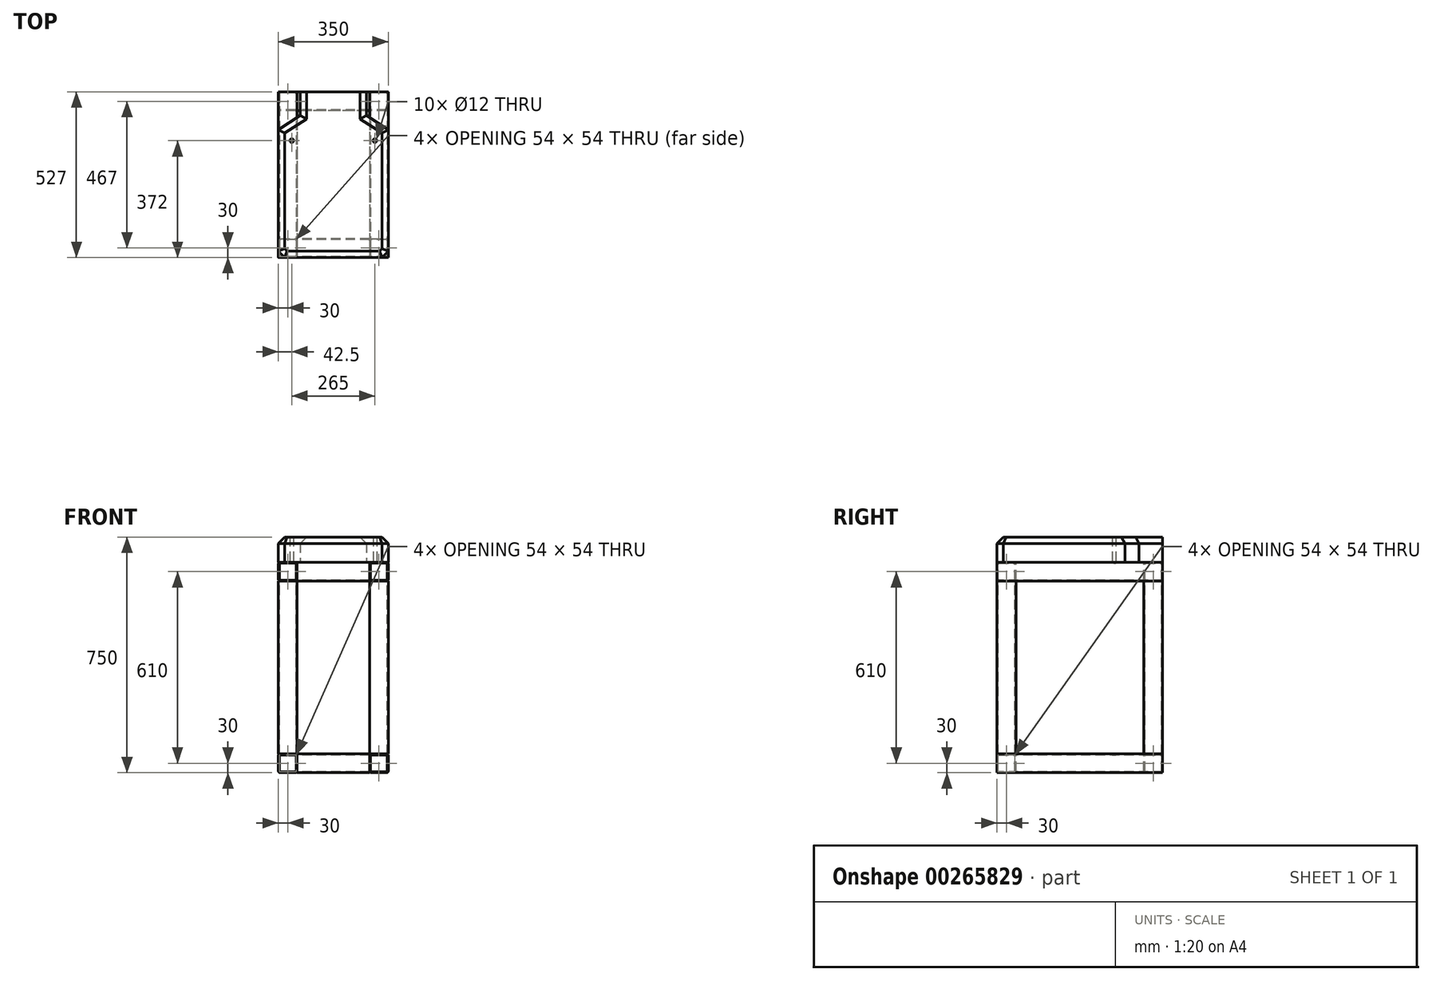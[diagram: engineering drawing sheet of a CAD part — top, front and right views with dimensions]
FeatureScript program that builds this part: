
annotation { "Feature Type Name" : "Feature", "Feature Type Description" : "" }
export const myFeature = defineFeature(function(context is Context, id is Id, definition is map)
    precondition{}
    {
        {
            var Q0;
            Q0=qCreatedBy(makeId("Top.planeOp"),FACE);
            var sketch = newSketch(context, id + "F0", { "sketchPlane" : qUnion([Q0])});
            skLineSegment(sketch, "E0.bottom", {"start": v(175, -263.5) * mm, "end": v(-175, -263.5) * mm});
            skLineSegment(sketch, "E0.top", {"start": v(105, 263.5) * mm, "end": v(-105, 263.5) * mm});
            skLineSegment(sketch, "E0.left", {"start": v(175, -263.5) * mm, "end": v(175, 143.5) * mm});
            skLineSegment(sketch, "E0.right", {"start": v(-175, -263.5) * mm, "end": v(-175, 143.5) * mm});
            skPoint(sketch, "E0.middle", {"position": v(0, 0) * mm});
            skCircle(sketch, "E1", {"center": v(-132.5, 108.5) * mm, "radius": 6 * mm});
            skCircle(sketch, "E2", {"center": v(132.5, 108.5) * mm, "radius": 6 * mm});
            skLineSegment(sketch, "E3", {"start": v(-175, 143.5) * mm, "end": v(-105, 188.5) * mm});
            skLineSegment(sketch, "E4", {"start": v(-105, 188.5) * mm, "end": v(-105, 263.5) * mm});
            skLineSegment(sketch, "E5", {"start": v(105, 263.5) * mm, "end": v(105, 188.5) * mm});
            skLineSegment(sketch, "E6", {"start": v(105, 188.5) * mm, "end": v(175, 143.5) * mm});
            skPoint(sketch, "E7.orphan", {"position": v(-175, 263.5) * mm});
            skPoint(sketch, "E8.orphan", {"position": v(175, 263.5) * mm});
            skSolve(sketch);
        }
        {
            var Q0;
            Q0 = qSketchRegion(id + "F0", true);
            extrude(context, id + "F1", {"entities" : qUnion([Q0]), "depth" : 80 * mm});
        }
        {
            var Q0;
            Q0=makeQuery(id+"F1.opExtrude","SWEPT_EDGE",EDGE,{"disambiguationData":[OSD([sQuery(id+"F0.wireOp",EDGE,"E0.bottom"),sQuery(id+"F0.wireOp",EDGE,"E0.right")])]});
            var Q1;
            Q1=makeQuery(id+"F1.opExtrude","SWEPT_EDGE",EDGE,{"disambiguationData":[OSD([sQuery(id+"F0.wireOp",EDGE,"E0.bottom"),sQuery(id+"F0.wireOp",EDGE,"E0.left")])]});
            chamfer(context, id + "F2", {"entities" : qUnion([Q0, Q1]), "width" : 20 * mm, "tangentPropagation" : true});
        }
        {
            var Q0;
            Q0=makeQuery(id+"F1.opExtrude","CAP_EDGE",EDGE,{"disambiguationData":[OSD([sQuery(id+"F0.wireOp",EDGE,"E0.right")])],"isStart":false});
            var Q1;
            Q1=makeQuery(id+"F1.opExtrude","CAP_EDGE",EDGE,{"disambiguationData":[OSD([sQuery(id+"F0.wireOp",EDGE,"E0.bottom")])],"isStart":false});
            var Q2;
            Q2=makeQuery(id+"F1.opExtrude","CAP_EDGE",EDGE,{"disambiguationData":[OSD([sQuery(id+"F0.wireOp",EDGE,"E0.left")])],"isStart":false});
            var Q3;
            {var subQ0=sQuery(id+"F0.wireOp",EDGE,"E0.left");var subQ1=sQuery(id+"F0.wireOp",EDGE,"E0.bottom");Q3=makeQuery(id+"F2.opChamfer","BLEND_EDGE",EDGE,{"blendedFrom":[makeQuery(id+"F1.opExtrude","SWEPT_EDGE",EDGE,{"disambiguationData":[OSD([subQ1,subQ0])]}),makeQuery(id+"F1.opExtrude","CAP_FACE",FACE,{"disambiguationData":[OSD([subQ1,sQuery(id+"F0.wireOp",EDGE,"E0.top"),subQ0,sQuery(id+"F0.wireOp",EDGE,"E0.right"),sQuery(id+"F0.wireOp",EDGE,"E1"),sQuery(id+"F0.wireOp",EDGE,"E2"),sQuery(id+"F0.wireOp",EDGE,"E3"),sQuery(id+"F0.wireOp",EDGE,"E4"),sQuery(id+"F0.wireOp",EDGE,"E5"),sQuery(id+"F0.wireOp",EDGE,"E6")])],"isStart":false})],"blendedInto":[makeQuery(id+"F1.opExtrude","CAP_FACE",FACE,{"disambiguationData":[OSD([subQ1,sQuery(id+"F0.wireOp",EDGE,"E0.top"),subQ0,sQuery(id+"F0.wireOp",EDGE,"E0.right"),sQuery(id+"F0.wireOp",EDGE,"E1"),sQuery(id+"F0.wireOp",EDGE,"E2"),sQuery(id+"F0.wireOp",EDGE,"E3"),sQuery(id+"F0.wireOp",EDGE,"E4"),sQuery(id+"F0.wireOp",EDGE,"E5"),sQuery(id+"F0.wireOp",EDGE,"E6")])],"isStart":false})]});}
            var Q4;
            {var subQ0=sQuery(id+"F0.wireOp",EDGE,"E0.right");var subQ1=sQuery(id+"F0.wireOp",EDGE,"E0.bottom");Q4=makeQuery(id+"F2.opChamfer","BLEND_EDGE",EDGE,{"blendedFrom":[makeQuery(id+"F1.opExtrude","SWEPT_EDGE",EDGE,{"disambiguationData":[OSD([subQ1,subQ0])]}),makeQuery(id+"F1.opExtrude","CAP_FACE",FACE,{"disambiguationData":[OSD([subQ1,sQuery(id+"F0.wireOp",EDGE,"E0.top"),sQuery(id+"F0.wireOp",EDGE,"E0.left"),subQ0,sQuery(id+"F0.wireOp",EDGE,"E1"),sQuery(id+"F0.wireOp",EDGE,"E2"),sQuery(id+"F0.wireOp",EDGE,"E3"),sQuery(id+"F0.wireOp",EDGE,"E4"),sQuery(id+"F0.wireOp",EDGE,"E5"),sQuery(id+"F0.wireOp",EDGE,"E6")])],"isStart":false})],"blendedInto":[makeQuery(id+"F1.opExtrude","CAP_FACE",FACE,{"disambiguationData":[OSD([subQ1,sQuery(id+"F0.wireOp",EDGE,"E0.top"),sQuery(id+"F0.wireOp",EDGE,"E0.left"),subQ0,sQuery(id+"F0.wireOp",EDGE,"E1"),sQuery(id+"F0.wireOp",EDGE,"E2"),sQuery(id+"F0.wireOp",EDGE,"E3"),sQuery(id+"F0.wireOp",EDGE,"E4"),sQuery(id+"F0.wireOp",EDGE,"E5"),sQuery(id+"F0.wireOp",EDGE,"E6")])],"isStart":false})]});}
            var Q5;
            Q5=makeQuery(id+"F1.opExtrude","CAP_EDGE",EDGE,{"disambiguationData":[OSD([sQuery(id+"F0.wireOp",EDGE,"E3")])],"isStart":false});
            var Q6;
            Q6=makeQuery(id+"F1.opExtrude","CAP_EDGE",EDGE,{"disambiguationData":[OSD([sQuery(id+"F0.wireOp",EDGE,"E4")])],"isStart":false});
            var Q7;
            Q7=makeQuery(id+"F1.opExtrude","CAP_EDGE",EDGE,{"disambiguationData":[OSD([sQuery(id+"F0.wireOp",EDGE,"E6")])],"isStart":false});
            var Q8;
            Q8=makeQuery(id+"F1.opExtrude","CAP_EDGE",EDGE,{"disambiguationData":[OSD([sQuery(id+"F0.wireOp",EDGE,"E5")])],"isStart":false});
            chamfer(context, id + "F3", {"entities" : qUnion([Q0, Q1, Q2, Q3, Q4, Q5, Q6, Q7, Q8]), "width" : 20 * mm, "tangentPropagation" : true});
        }
        {
            var Q0;
            Q0=makeQuery(id+"F1.opExtrude","SWEPT_FACE",FACE,{"disambiguationData":[OSD([sQuery(id+"F0.wireOp",EDGE,"E0.bottom")])]});
            var sketch = newSketch(context, id + "F4", { "sketchPlane" : qUnion([Q0])});
            skLineSegment(sketch, "E9.bottom", {"start": v(121, 0) * mm, "end": v(169, 0) * mm});
            skLineSegment(sketch, "E9.top", {"start": v(121, -60) * mm, "end": v(169, -60) * mm});
            skLineSegment(sketch, "E9.left", {"start": v(115, -6) * mm, "end": v(115, -54) * mm});
            skLineSegment(sketch, "E9.right", {"start": v(175, -6) * mm, "end": v(175, -54) * mm});
            skPoint(sketch, "E10.visualSharp", {"position": v(175, 0) * mm});
            skArc(sketch, "E10.filletArc", {"start": v(175, -6) * mm, "mid": v(173.24, -1.76) * mm, "end": v(169, 0) * mm});
            skPoint(sketch, "E11.visualSharp", {"position": v(175, -60) * mm});
            skArc(sketch, "E11.filletArc", {"start": v(169, -60) * mm, "mid": v(173.24, -58.24) * mm, "end": v(175, -54) * mm});
            skPoint(sketch, "E12.visualSharp", {"position": v(115, -60) * mm});
            skArc(sketch, "E12.filletArc", {"start": v(115, -54) * mm, "mid": v(116.76, -58.24) * mm, "end": v(121, -60) * mm});
            skPoint(sketch, "E13.visualSharp", {"position": v(115, 0) * mm});
            skArc(sketch, "E13.filletArc", {"start": v(121, 0) * mm, "mid": v(116.76, -1.76) * mm, "end": v(115, -6) * mm});
            skArc(sketch, "E14.0", {"start": v(172, -6) * mm, "mid": v(171.12, -3.88) * mm, "end": v(169, -3) * mm});
            skLineSegment(sketch, "E14.1", {"start": v(121, -3) * mm, "end": v(169, -3) * mm});
            skLineSegment(sketch, "E14.2", {"start": v(172, -6) * mm, "end": v(172, -54) * mm});
            skArc(sketch, "E14.3", {"start": v(121, -3) * mm, "mid": v(118.88, -3.88) * mm, "end": v(118, -6) * mm});
            skArc(sketch, "E14.4", {"start": v(169, -57) * mm, "mid": v(171.12, -56.12) * mm, "end": v(172, -54) * mm});
            skLineSegment(sketch, "E14.5", {"start": v(121, -57) * mm, "end": v(169, -57) * mm});
            skArc(sketch, "E14.6", {"start": v(118, -54) * mm, "mid": v(118.88, -56.12) * mm, "end": v(121, -57) * mm});
            skLineSegment(sketch, "E14.7", {"start": v(118, -6) * mm, "end": v(118, -54) * mm});
            skSolve(sketch);
        }
        {
            var Q0;
            Q0 = qSketchRegion(id + "F4", true);
            extrude(context, id + "F5", {"entities" : qUnion([Q0]), "oppositeDirection" : true, "depth" : 527 * mm});
        }
        {
            var Q0;
            Q0=makeQuery(id+"F5.opExtrude","SWEPT_BODY",BODY,{"disambiguationData":[OSD([sQuery(id+"F4.wireOp",EDGE,"E9.bottom"),sQuery(id+"F4.wireOp",EDGE,"E9.top"),sQuery(id+"F4.wireOp",EDGE,"E9.left"),sQuery(id+"F4.wireOp",EDGE,"E9.right"),sQuery(id+"F4.wireOp",EDGE,"E10.filletArc"),sQuery(id+"F4.wireOp",EDGE,"E11.filletArc"),sQuery(id+"F4.wireOp",EDGE,"E12.filletArc"),sQuery(id+"F4.wireOp",EDGE,"E13.filletArc"),sQuery(id+"F4.wireOp",EDGE,"E14.0"),sQuery(id+"F4.wireOp",EDGE,"E14.1"),sQuery(id+"F4.wireOp",EDGE,"E14.2"),sQuery(id+"F4.wireOp",EDGE,"E14.3"),sQuery(id+"F4.wireOp",EDGE,"E14.4"),sQuery(id+"F4.wireOp",EDGE,"E14.5"),sQuery(id+"F4.wireOp",EDGE,"E14.6"),sQuery(id+"F4.wireOp",EDGE,"E14.7")])]});
            transform(context, id + "F6", {"entities" : qUnion([Q0]), "transformType" : TransformType.TRANSLATION_3D, "dx" : -290 * mm, "dy" : 0 * mm, "dz" : 0 * mm, "makeCopy" : true});
        }
        {
            var Q0;
            Q0=makeQuery(id+"F6.opPattern","COPY",FACE,{"derivedFrom":makeQuery(id+"F5.opExtrude","SWEPT_FACE",FACE,{"disambiguationData":[OSD([sQuery(id+"F4.wireOp",EDGE,"E9.right")])]}),"instanceName":"1"});
            var sketch = newSketch(context, id + "F7", { "sketchPlane" : qUnion([Q0])});
            skPoint(sketch, "E15.firstSnap0", {"position": v(263.5, -30) * mm});
            skLineSegment(sketch, "E15.bottom", {"start": v(257.5, 0) * mm, "end": v(209.5, 0) * mm});
            skLineSegment(sketch, "E15.top", {"start": v(257.5, -60) * mm, "end": v(209.5, -60) * mm});
            skLineSegment(sketch, "E15.left", {"start": v(263.5, -6) * mm, "end": v(263.5, -54) * mm});
            skLineSegment(sketch, "E15.right", {"start": v(203.5, -6) * mm, "end": v(203.5, -54) * mm});
            skPoint(sketch, "E16.visualSharp", {"position": v(263.5, -60) * mm});
            skArc(sketch, "E16.filletArc", {"start": v(257.5, -60) * mm, "mid": v(261.74, -58.24) * mm, "end": v(263.5, -54) * mm});
            skPoint(sketch, "E17.visualSharp", {"position": v(203.5, -60) * mm});
            skArc(sketch, "E17.filletArc", {"start": v(203.5, -54) * mm, "mid": v(205.26, -58.24) * mm, "end": v(209.5, -60) * mm});
            skPoint(sketch, "E18.visualSharp", {"position": v(203.5, 0) * mm});
            skArc(sketch, "E18.filletArc", {"start": v(209.5, 0) * mm, "mid": v(205.26, -1.76) * mm, "end": v(203.5, -6) * mm});
            skPoint(sketch, "E19.visualSharp", {"position": v(263.5, 0) * mm});
            skArc(sketch, "E19.filletArc", {"start": v(263.5, -6) * mm, "mid": v(261.74, -1.76) * mm, "end": v(257.5, 0) * mm});
            skArc(sketch, "E20.0", {"start": v(257.5, -57) * mm, "mid": v(259.62, -56.12) * mm, "end": v(260.5, -54) * mm});
            skLineSegment(sketch, "E20.1", {"start": v(260.5, -6) * mm, "end": v(260.5, -54) * mm});
            skLineSegment(sketch, "E20.2", {"start": v(257.5, -57) * mm, "end": v(209.5, -57) * mm});
            skArc(sketch, "E20.3", {"start": v(260.5, -6) * mm, "mid": v(259.62, -3.88) * mm, "end": v(257.5, -3) * mm});
            skArc(sketch, "E20.4", {"start": v(206.5, -54) * mm, "mid": v(207.38, -56.12) * mm, "end": v(209.5, -57) * mm});
            skLineSegment(sketch, "E20.5", {"start": v(206.5, -6) * mm, "end": v(206.5, -54) * mm});
            skArc(sketch, "E20.6", {"start": v(209.5, -3) * mm, "mid": v(207.38, -3.88) * mm, "end": v(206.5, -6) * mm});
            skLineSegment(sketch, "E20.7", {"start": v(257.5, -3) * mm, "end": v(209.5, -3) * mm});
            skSolve(sketch);
        }
        {
            var Q0;
            Q0 = qSketchRegion(id + "F7", true);
            var Q1;
            Q1=makeQuery(id+"F5.opExtrude","SWEPT_FACE",FACE,{"disambiguationData":[OSD([sQuery(id+"F4.wireOp",EDGE,"E9.left")])]});
            extrude(context, id + "F8", {"entities" : qUnion([Q0]), "endBound" : BoundingType.UP_TO_SURFACE, "endBoundEntityFace" : qUnion([Q1]), "depth" : 25 * mm});
        }
        {
            var Q0;
            Q0=makeQuery(id+"F8.opExtrude","SWEPT_BODY",BODY,{"disambiguationData":[OSD([sQuery(id+"F7.wireOp",EDGE,"E15.bottom"),sQuery(id+"F7.wireOp",EDGE,"E15.top"),sQuery(id+"F7.wireOp",EDGE,"E15.left"),sQuery(id+"F7.wireOp",EDGE,"E15.right"),sQuery(id+"F7.wireOp",EDGE,"E16.filletArc"),sQuery(id+"F7.wireOp",EDGE,"E17.filletArc"),sQuery(id+"F7.wireOp",EDGE,"E18.filletArc"),sQuery(id+"F7.wireOp",EDGE,"E19.filletArc"),sQuery(id+"F7.wireOp",EDGE,"E20.0"),sQuery(id+"F7.wireOp",EDGE,"E20.1"),sQuery(id+"F7.wireOp",EDGE,"E20.2"),sQuery(id+"F7.wireOp",EDGE,"E20.3"),sQuery(id+"F7.wireOp",EDGE,"E20.4"),sQuery(id+"F7.wireOp",EDGE,"E20.5"),sQuery(id+"F7.wireOp",EDGE,"E20.6"),sQuery(id+"F7.wireOp",EDGE,"E20.7")])]});
            transform(context, id + "F9", {"entities" : qUnion([Q0]), "transformType" : TransformType.TRANSLATION_3D, "dx" : 0 * mm, "dy" : -467 * mm, "dz" : 0 * mm, "makeCopy" : true});
        }
        {
            var Q0;
            Q0=makeQuery(id+"F5.opExtrude","SWEPT_FACE",FACE,{"disambiguationData":[OSD([sQuery(id+"F4.wireOp",EDGE,"E9.bottom")])]});
            var sketch = newSketch(context, id + "F10", { "sketchPlane" : qUnion([Q0])});
            skCircle(sketch, "E21", {"center": v(132.5, 108.5) * mm, "radius": 6 * mm});
            skSolve(sketch);
        }
        {
            var Q0;
            Q0=makeQuery(id+"F6.opPattern","COPY",FACE,{"derivedFrom":makeQuery(id+"F5.opExtrude","SWEPT_FACE",FACE,{"disambiguationData":[OSD([sQuery(id+"F4.wireOp",EDGE,"E9.bottom")])]}),"instanceName":"1"});
            var sketch = newSketch(context, id + "F11", { "sketchPlane" : qUnion([Q0])});
            skCircle(sketch, "E22", {"center": v(-132.5, 108.5) * mm, "radius": 6 * mm});
            skSolve(sketch);
        }
        {
            var Q0;
            Q0=makeQuery(id+"F5.opExtrude","SWEPT_BODY",BODY,{"disambiguationData":[OSD([sQuery(id+"F4.wireOp",EDGE,"E9.bottom"),sQuery(id+"F4.wireOp",EDGE,"E9.top"),sQuery(id+"F4.wireOp",EDGE,"E9.left"),sQuery(id+"F4.wireOp",EDGE,"E9.right"),sQuery(id+"F4.wireOp",EDGE,"E10.filletArc"),sQuery(id+"F4.wireOp",EDGE,"E11.filletArc"),sQuery(id+"F4.wireOp",EDGE,"E12.filletArc"),sQuery(id+"F4.wireOp",EDGE,"E13.filletArc"),sQuery(id+"F4.wireOp",EDGE,"E14.0"),sQuery(id+"F4.wireOp",EDGE,"E14.1"),sQuery(id+"F4.wireOp",EDGE,"E14.2"),sQuery(id+"F4.wireOp",EDGE,"E14.3"),sQuery(id+"F4.wireOp",EDGE,"E14.4"),sQuery(id+"F4.wireOp",EDGE,"E14.5"),sQuery(id+"F4.wireOp",EDGE,"E14.6"),sQuery(id+"F4.wireOp",EDGE,"E14.7")])]});
            transform(context, id + "F12", {"entities" : qUnion([Q0]), "transformType" : TransformType.TRANSLATION_3D, "dx" : 0 * mm, "dy" : 0 * mm, "dz" : -610 * mm, "makeCopy" : true});
        }
        {
            var Q0;
            Q0=makeQuery(id+"F6.opPattern","COPY",BODY,{"derivedFrom":makeQuery(id+"F5.opExtrude","SWEPT_BODY",BODY,{"disambiguationData":[OSD([sQuery(id+"F4.wireOp",EDGE,"E9.bottom"),sQuery(id+"F4.wireOp",EDGE,"E9.top"),sQuery(id+"F4.wireOp",EDGE,"E9.left"),sQuery(id+"F4.wireOp",EDGE,"E9.right"),sQuery(id+"F4.wireOp",EDGE,"E10.filletArc"),sQuery(id+"F4.wireOp",EDGE,"E11.filletArc"),sQuery(id+"F4.wireOp",EDGE,"E12.filletArc"),sQuery(id+"F4.wireOp",EDGE,"E13.filletArc"),sQuery(id+"F4.wireOp",EDGE,"E14.0"),sQuery(id+"F4.wireOp",EDGE,"E14.1"),sQuery(id+"F4.wireOp",EDGE,"E14.2"),sQuery(id+"F4.wireOp",EDGE,"E14.3"),sQuery(id+"F4.wireOp",EDGE,"E14.4"),sQuery(id+"F4.wireOp",EDGE,"E14.5"),sQuery(id+"F4.wireOp",EDGE,"E14.6"),sQuery(id+"F4.wireOp",EDGE,"E14.7")])]}),"instanceName":"1"});
            transform(context, id + "F13", {"entities" : qUnion([Q0]), "transformType" : TransformType.TRANSLATION_3D, "dx" : 0 * mm, "dy" : 0 * mm, "dz" : -610 * mm, "makeCopy" : true});
        }
        {
            var Q0;
            Q0 = qSketchRegion(id + "F10", true);
            extrude(context, id + "F14", {"entities" : qUnion([Q0]), "operationType" : NewBodyOperationType.REMOVE, "endBound" : BoundingType.THROUGH_ALL, "oppositeDirection" : true, "depth" : 25 * mm});
        }
        {
            var Q0;
            Q0 = qSketchRegion(id + "F11", true);
            extrude(context, id + "F15", {"entities" : qUnion([Q0]), "operationType" : NewBodyOperationType.REMOVE, "endBound" : BoundingType.THROUGH_ALL, "oppositeDirection" : true, "depth" : 25 * mm});
        }
        {
            var Q0;
            Q0=makeQuery(id+"F9.opPattern","COPY",BODY,{"derivedFrom":makeQuery(id+"F8.opExtrude","SWEPT_BODY",BODY,{"disambiguationData":[OSD([sQuery(id+"F7.wireOp",EDGE,"E15.bottom"),sQuery(id+"F7.wireOp",EDGE,"E15.top"),sQuery(id+"F7.wireOp",EDGE,"E15.left"),sQuery(id+"F7.wireOp",EDGE,"E15.right"),sQuery(id+"F7.wireOp",EDGE,"E16.filletArc"),sQuery(id+"F7.wireOp",EDGE,"E17.filletArc"),sQuery(id+"F7.wireOp",EDGE,"E18.filletArc"),sQuery(id+"F7.wireOp",EDGE,"E19.filletArc"),sQuery(id+"F7.wireOp",EDGE,"E20.0"),sQuery(id+"F7.wireOp",EDGE,"E20.1"),sQuery(id+"F7.wireOp",EDGE,"E20.2"),sQuery(id+"F7.wireOp",EDGE,"E20.3"),sQuery(id+"F7.wireOp",EDGE,"E20.4"),sQuery(id+"F7.wireOp",EDGE,"E20.5"),sQuery(id+"F7.wireOp",EDGE,"E20.6"),sQuery(id+"F7.wireOp",EDGE,"E20.7")])]}),"instanceName":"1"});
            transform(context, id + "F16", {"entities" : qUnion([Q0]), "transformType" : TransformType.TRANSLATION_3D, "dx" : 0 * mm, "dy" : 0 * mm, "dz" : -610 * mm, "makeCopy" : true});
        }
        {
            var Q0;
            Q0=makeQuery(id+"F8.opExtrude","SWEPT_BODY",BODY,{"disambiguationData":[OSD([sQuery(id+"F7.wireOp",EDGE,"E15.bottom"),sQuery(id+"F7.wireOp",EDGE,"E15.top"),sQuery(id+"F7.wireOp",EDGE,"E15.left"),sQuery(id+"F7.wireOp",EDGE,"E15.right"),sQuery(id+"F7.wireOp",EDGE,"E16.filletArc"),sQuery(id+"F7.wireOp",EDGE,"E17.filletArc"),sQuery(id+"F7.wireOp",EDGE,"E18.filletArc"),sQuery(id+"F7.wireOp",EDGE,"E19.filletArc"),sQuery(id+"F7.wireOp",EDGE,"E20.0"),sQuery(id+"F7.wireOp",EDGE,"E20.1"),sQuery(id+"F7.wireOp",EDGE,"E20.2"),sQuery(id+"F7.wireOp",EDGE,"E20.3"),sQuery(id+"F7.wireOp",EDGE,"E20.4"),sQuery(id+"F7.wireOp",EDGE,"E20.5"),sQuery(id+"F7.wireOp",EDGE,"E20.6"),sQuery(id+"F7.wireOp",EDGE,"E20.7")])]});
            transform(context, id + "F17", {"entities" : qUnion([Q0]), "transformType" : TransformType.TRANSLATION_3D, "dx" : 0 * mm, "dy" : 0 * mm, "dz" : -610 * mm, "makeCopy" : true});
        }
        {
            var Q0;
            Q0=makeQuery(id+"F5.opExtrude","SWEPT_FACE",FACE,{"disambiguationData":[OSD([sQuery(id+"F4.wireOp",EDGE,"E9.top")])]});
            var sketch = newSketch(context, id + "F18", { "sketchPlane" : qUnion([Q0])});
            skPoint(sketch, "E23.firstSnap0", {"position": v(145, -263.5) * mm});
            skLineSegment(sketch, "E23.bottom", {"start": v(169, -263.5) * mm, "end": v(121, -263.5) * mm});
            skLineSegment(sketch, "E23.top", {"start": v(169, -203.5) * mm, "end": v(121, -203.5) * mm});
            skLineSegment(sketch, "E23.left", {"start": v(175, -257.5) * mm, "end": v(175, -209.5) * mm});
            skLineSegment(sketch, "E23.right", {"start": v(115, -257.5) * mm, "end": v(115, -209.5) * mm});
            skPoint(sketch, "E24.visualSharp", {"position": v(175, -263.5) * mm});
            skArc(sketch, "E24.filletArc", {"start": v(169, -263.5) * mm, "mid": v(173.24, -261.74) * mm, "end": v(175, -257.5) * mm});
            skPoint(sketch, "E25.visualSharp", {"position": v(175, -203.5) * mm});
            skArc(sketch, "E25.filletArc", {"start": v(175, -209.5) * mm, "mid": v(173.24, -205.26) * mm, "end": v(169, -203.5) * mm});
            skPoint(sketch, "E26.visualSharp", {"position": v(115, -203.5) * mm});
            skArc(sketch, "E26.filletArc", {"start": v(121, -203.5) * mm, "mid": v(116.76, -205.26) * mm, "end": v(115, -209.5) * mm});
            skPoint(sketch, "E27.visualSharp", {"position": v(115, -263.5) * mm});
            skArc(sketch, "E27.filletArc", {"start": v(115, -257.5) * mm, "mid": v(116.76, -261.74) * mm, "end": v(121, -263.5) * mm});
            skArc(sketch, "E28.0", {"start": v(118, -257.5) * mm, "mid": v(118.88, -259.62) * mm, "end": v(121, -260.5) * mm});
            skLineSegment(sketch, "E28.1", {"start": v(169, -260.5) * mm, "end": v(121, -260.5) * mm});
            skLineSegment(sketch, "E28.2", {"start": v(118, -257.5) * mm, "end": v(118, -209.5) * mm});
            skArc(sketch, "E28.3", {"start": v(169, -260.5) * mm, "mid": v(171.12, -259.62) * mm, "end": v(172, -257.5) * mm});
            skArc(sketch, "E28.4", {"start": v(121, -206.5) * mm, "mid": v(118.88, -207.38) * mm, "end": v(118, -209.5) * mm});
            skLineSegment(sketch, "E28.5", {"start": v(169, -206.5) * mm, "end": v(121, -206.5) * mm});
            skArc(sketch, "E28.6", {"start": v(172, -209.5) * mm, "mid": v(171.12, -207.38) * mm, "end": v(169, -206.5) * mm});
            skLineSegment(sketch, "E28.7", {"start": v(172, -257.5) * mm, "end": v(172, -209.5) * mm});
            skSolve(sketch);
        }
        {
            var Q0;
            Q0 = qSketchRegion(id + "F18", true);
            var Q1;
            Q1=makeQuery(id+"F12.opPattern","COPY",FACE,{"derivedFrom":makeQuery(id+"F5.opExtrude","SWEPT_FACE",FACE,{"disambiguationData":[OSD([sQuery(id+"F4.wireOp",EDGE,"E9.bottom")])]}),"instanceName":"1"});
            extrude(context, id + "F19", {"entities" : qUnion([Q0]), "endBound" : BoundingType.UP_TO_SURFACE, "endBoundEntityFace" : qUnion([Q1]), "depth" : 25 * mm});
        }
        {
            var Q0;
            Q0=makeQuery(id+"F19.opExtrude","SWEPT_BODY",BODY,{"disambiguationData":[OSD([sQuery(id+"F18.wireOp",EDGE,"E23.bottom"),sQuery(id+"F18.wireOp",EDGE,"E23.top"),sQuery(id+"F18.wireOp",EDGE,"E23.left"),sQuery(id+"F18.wireOp",EDGE,"E23.right"),sQuery(id+"F18.wireOp",EDGE,"E24.filletArc"),sQuery(id+"F18.wireOp",EDGE,"E25.filletArc"),sQuery(id+"F18.wireOp",EDGE,"E26.filletArc"),sQuery(id+"F18.wireOp",EDGE,"E27.filletArc"),sQuery(id+"F18.wireOp",EDGE,"E28.0"),sQuery(id+"F18.wireOp",EDGE,"E28.1"),sQuery(id+"F18.wireOp",EDGE,"E28.2"),sQuery(id+"F18.wireOp",EDGE,"E28.3"),sQuery(id+"F18.wireOp",EDGE,"E28.4"),sQuery(id+"F18.wireOp",EDGE,"E28.5"),sQuery(id+"F18.wireOp",EDGE,"E28.6"),sQuery(id+"F18.wireOp",EDGE,"E28.7")])]});
            transform(context, id + "F20", {"entities" : qUnion([Q0]), "transformType" : TransformType.TRANSLATION_3D, "dx" : -290 * mm, "dy" : 0 * mm, "dz" : 0 * mm, "makeCopy" : true});
        }
        {
            var Q0;
            Q0=makeQuery(id+"F19.opExtrude","SWEPT_BODY",BODY,{"disambiguationData":[OSD([sQuery(id+"F18.wireOp",EDGE,"E23.bottom"),sQuery(id+"F18.wireOp",EDGE,"E23.top"),sQuery(id+"F18.wireOp",EDGE,"E23.left"),sQuery(id+"F18.wireOp",EDGE,"E23.right"),sQuery(id+"F18.wireOp",EDGE,"E24.filletArc"),sQuery(id+"F18.wireOp",EDGE,"E25.filletArc"),sQuery(id+"F18.wireOp",EDGE,"E26.filletArc"),sQuery(id+"F18.wireOp",EDGE,"E27.filletArc"),sQuery(id+"F18.wireOp",EDGE,"E28.0"),sQuery(id+"F18.wireOp",EDGE,"E28.1"),sQuery(id+"F18.wireOp",EDGE,"E28.2"),sQuery(id+"F18.wireOp",EDGE,"E28.3"),sQuery(id+"F18.wireOp",EDGE,"E28.4"),sQuery(id+"F18.wireOp",EDGE,"E28.5"),sQuery(id+"F18.wireOp",EDGE,"E28.6"),sQuery(id+"F18.wireOp",EDGE,"E28.7")])]});
            transform(context, id + "F21", {"entities" : qUnion([Q0]), "transformType" : TransformType.TRANSLATION_3D, "dx" : 0 * mm, "dy" : -467 * mm, "dz" : 0 * mm, "makeCopy" : true});
        }
        {
            var Q0;
            Q0=makeQuery(id+"F21.opPattern","COPY",BODY,{"derivedFrom":makeQuery(id+"F19.opExtrude","SWEPT_BODY",BODY,{"disambiguationData":[OSD([sQuery(id+"F18.wireOp",EDGE,"E23.bottom"),sQuery(id+"F18.wireOp",EDGE,"E23.top"),sQuery(id+"F18.wireOp",EDGE,"E23.left"),sQuery(id+"F18.wireOp",EDGE,"E23.right"),sQuery(id+"F18.wireOp",EDGE,"E24.filletArc"),sQuery(id+"F18.wireOp",EDGE,"E25.filletArc"),sQuery(id+"F18.wireOp",EDGE,"E26.filletArc"),sQuery(id+"F18.wireOp",EDGE,"E27.filletArc"),sQuery(id+"F18.wireOp",EDGE,"E28.0"),sQuery(id+"F18.wireOp",EDGE,"E28.1"),sQuery(id+"F18.wireOp",EDGE,"E28.2"),sQuery(id+"F18.wireOp",EDGE,"E28.3"),sQuery(id+"F18.wireOp",EDGE,"E28.4"),sQuery(id+"F18.wireOp",EDGE,"E28.5"),sQuery(id+"F18.wireOp",EDGE,"E28.6"),sQuery(id+"F18.wireOp",EDGE,"E28.7")])]}),"instanceName":"1"});
            transform(context, id + "F22", {"entities" : qUnion([Q0]), "transformType" : TransformType.TRANSLATION_3D, "dx" : -290 * mm, "dy" : 0 * mm, "dz" : 0 * mm, "makeCopy" : true});
        }
    });
